# Revit family: Телевизор 42
name_source: partatom
category: Оборудование
revit_build: Autodesk Revit 2017 (Build: 20170118_1100(x64)
units: mm (PartAtom-declared; Revit-internal decimal feet)

## family parameters
Всегда вертикально = Да
На основе рабочей плоскости = Нет
Общий = Нет
При загрузке вырезать с полостями = Нет
Размер круглого соединителя = Использовать диаметр
Тип детали = Нормальный
Точка расчета площади = Нет

## types (2) — shared parameters
Группа модели = ТХ
Общ_Высота = 635 мм
Общ_Глубина = 60 мм
Общ_Задание = СС, ЭМ
Общ_Масса = 10
Общ_Мощность номинальная = 150 Вт
Общ_Напряжение = 220 В
Общ_Ширина = 1023 мм

## per-type parameters (varying)
| type | Изготовитель | Общ_Единицы измерения | Общ_Наименование | Подставка |
| На настенном кронштейне | Severin | компл. | ЖК-телевизор 42'' в комплекте с настенным кронштейном | Нет |
| На подставке |  | шт. | ЖК-телевизор 42" | Да |

## geometry (parser evidence)
native form markers: Blend x12
no freeform markers — native parametric forms only
